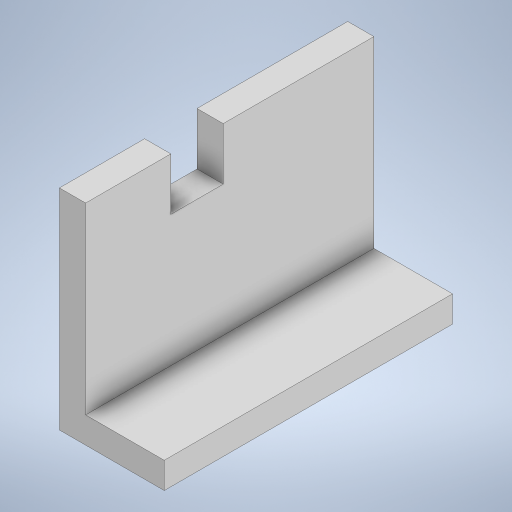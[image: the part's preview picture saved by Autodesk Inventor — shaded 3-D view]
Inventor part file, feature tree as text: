
AUTODESK INVENTOR PART (.ipt)
format: ipt  version: 2023 (Build 270158000, 158)  size: 210,944 bytes
history: native  units: in
note: dims shown in document units (in); Inventor stores cm internally (conversion verified against a paired STEP export)
features: extrude x2, sketch x2
ambient origin geometry x8: Origin, YZ Plane, XZ Plane, XY Plane, X Axis, Y Axis, Z Axis, Center Point
bodies: Solid1 (feature_tree)
feature tree (4):
  extrude  "Extrusion1"  Depth=0.6299in
  extrude  "Extrusion2"  Depth=0.8661in TaperAngle=0.0deg
  sketch  "Sketch1"  dims[d0=0.0787in d1=0.6299in]
  sketch  "Sketch2"  dims[d2=0.2362in d3=0.8661in d4=0.0in d5=0.1575in d6=0.1575in d7=0.3937in d8=0.0in]
